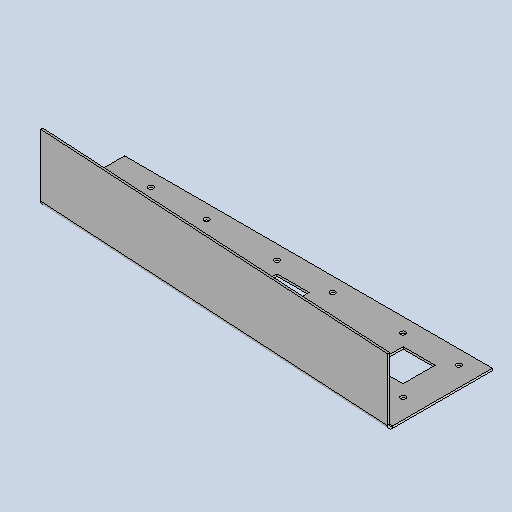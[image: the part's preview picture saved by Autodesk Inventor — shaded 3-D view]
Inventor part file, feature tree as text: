
AUTODESK INVENTOR PART (.ipt)
format: ipt  version: 2025.3 (Build 293356030, 356C)  size: 255,488 bytes
history: native  units: mm
features: sheet_metal_op x4, sketch x3, other x3, extrude x1, pattern_linear x1
ambient origin geometry x8: Origin, YZ Plane, XZ Plane, XY Plane, X Axis, Y Axis, Z Axis, Center Point
bodies: Solid1 (feature_tree)
feature tree (12):
  sheet_metal_op  "Face1"
  extrude  "Extrusion2"  Depth=2.0mm
  sheet_metal_op  "Flange3"
  pattern_linear  "Rectangular Pattern2"  Count1=8  [1 undecoded]
  sketch  "Sketch1"  dims[d2=2.0mm d32=100.0mm d60=80.0mm]
  other  "Plate1"
  sketch  "Sketch9"  dims[d61=350.0mm]
  other  "Plate4"
  sheet_metal_op  "Bend3"
  sheet_metal_op  "Corner3"
  sketch  "Sketch11"  dims[d62=2.0mm d63=1.0mm d64=4.0mm d65=2.75mm d66=64.0mm d67=90.0deg d68=2.75mm d69=8.0mm d70=2.0mm d71=2.75mm d86=30.0mm d87=30.0mm d88=30.5mm d89=30.5mm d90=5.0mm d92=15.933243mm d93=30.0mm d94=30.0mm d95=45.0mm d97=0.0mm d98=0.0mm d99=30.0mm d101=120.0mm d103=40.0mm d104=75.0mm]
  other  "Definition1"
note: 1 required parameter value undecoded (feature->parameter linkage not recoverable at this tier; creation-order binding heuristic only, values carry confidence <= 0.55)
